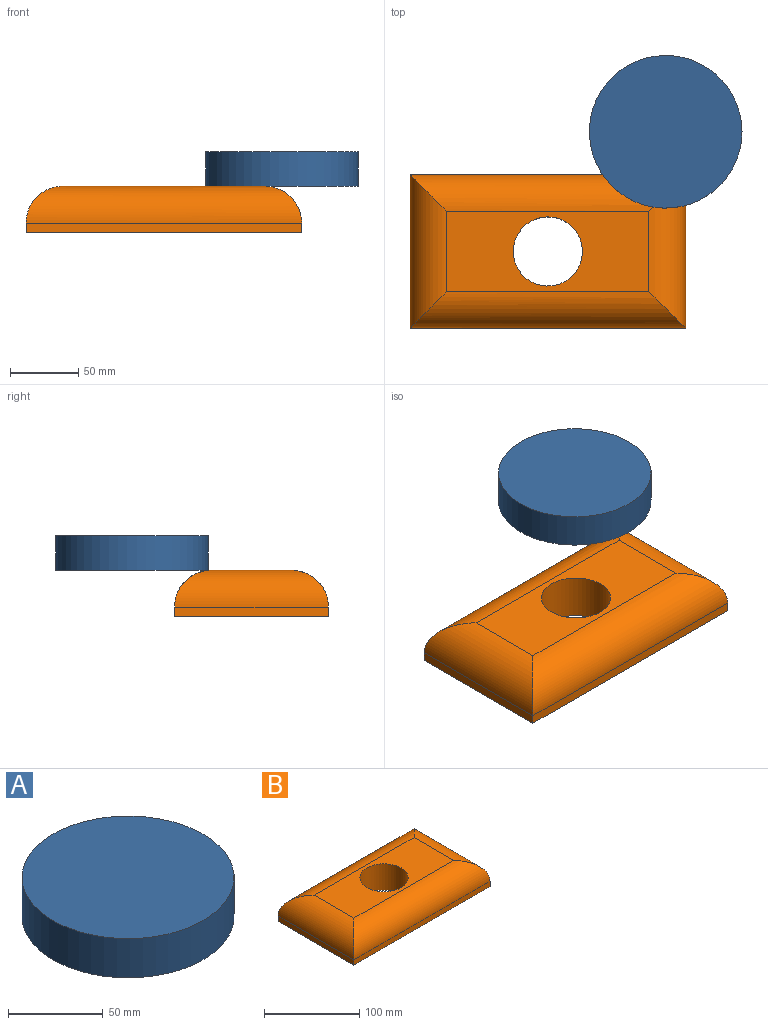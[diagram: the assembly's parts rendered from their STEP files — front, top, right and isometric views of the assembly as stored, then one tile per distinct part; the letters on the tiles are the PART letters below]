
ASSEMBLY  parts=2 mates=1
PART A: 3 faces, bbox 112.1x112.1x25.4 mm
  f0: cylinder r=56.06mm len=112.13mm, axis (0,0,-1), area 8947.5mm2, adj f1,f2
  f1: plane 112.13x112.13mm, normal (0,0,1), area 9874.7mm2, adj f0
  f2: plane 112.13x112.13mm, normal (0,0,-1), area 9874.7mm2, adj f0
PART B: 11 faces, bbox 202.5x113x33.8 mm
  f0: plane 202.48x6.8mm, normal (0,-1,0), area 1377mm2, adj f1,f3,f5,f6
  f1: plane 113.04x6.8mm, normal (1,0,0), area 768.7mm2, adj f0,f2,f5,f7
  f2: plane 202.48x6.8mm, normal (0,1,0), area 1377mm2, adj f1,f3,f5,f9
  f3: plane 113.04x6.8mm, normal (-1,0,0), area 768.7mm2, adj f0,f2,f5,f8
  f4: plane 148.52x59.07mm, normal (0,0,1), area 6746.7mm2, adj f6,f7,f8,f9,f10
  f5: plane 202.48x113.04mm, normal (0,0,-1), area 20860.9mm2, adj f0,f1,f2,f3,f10
  f6: cylinder r=26.98mm len=202.48mm, axis (-1,0,0), area 7750.6mm2, adj f0,f4,f7,f8
  f7: cylinder r=26.98mm len=113.04mm, axis (0,-1,0), area 3959.6mm2, adj f1,f4,f6,f9
  f8: cylinder r=26.98mm len=113.04mm, axis (0,1,0), area 3959.6mm2, adj f3,f4,f6,f9
  f9: cylinder r=26.98mm len=202.48mm, axis (1,0,0), area 7750.6mm2, adj f2,f4,f7,f8
  f10: cylinder r=25.4mm len=50.8mm, axis (0,0,1), area 5391.4mm2, adj f4,f5
PLACE A t=(120.93,160.09,56.8)mm
PLACE B t=(34.31,66.14,23.02)mm
MATE planar B.f10 <-> A.f0  axis (0,0,1) through (34.31,66.14,56.8)mm
